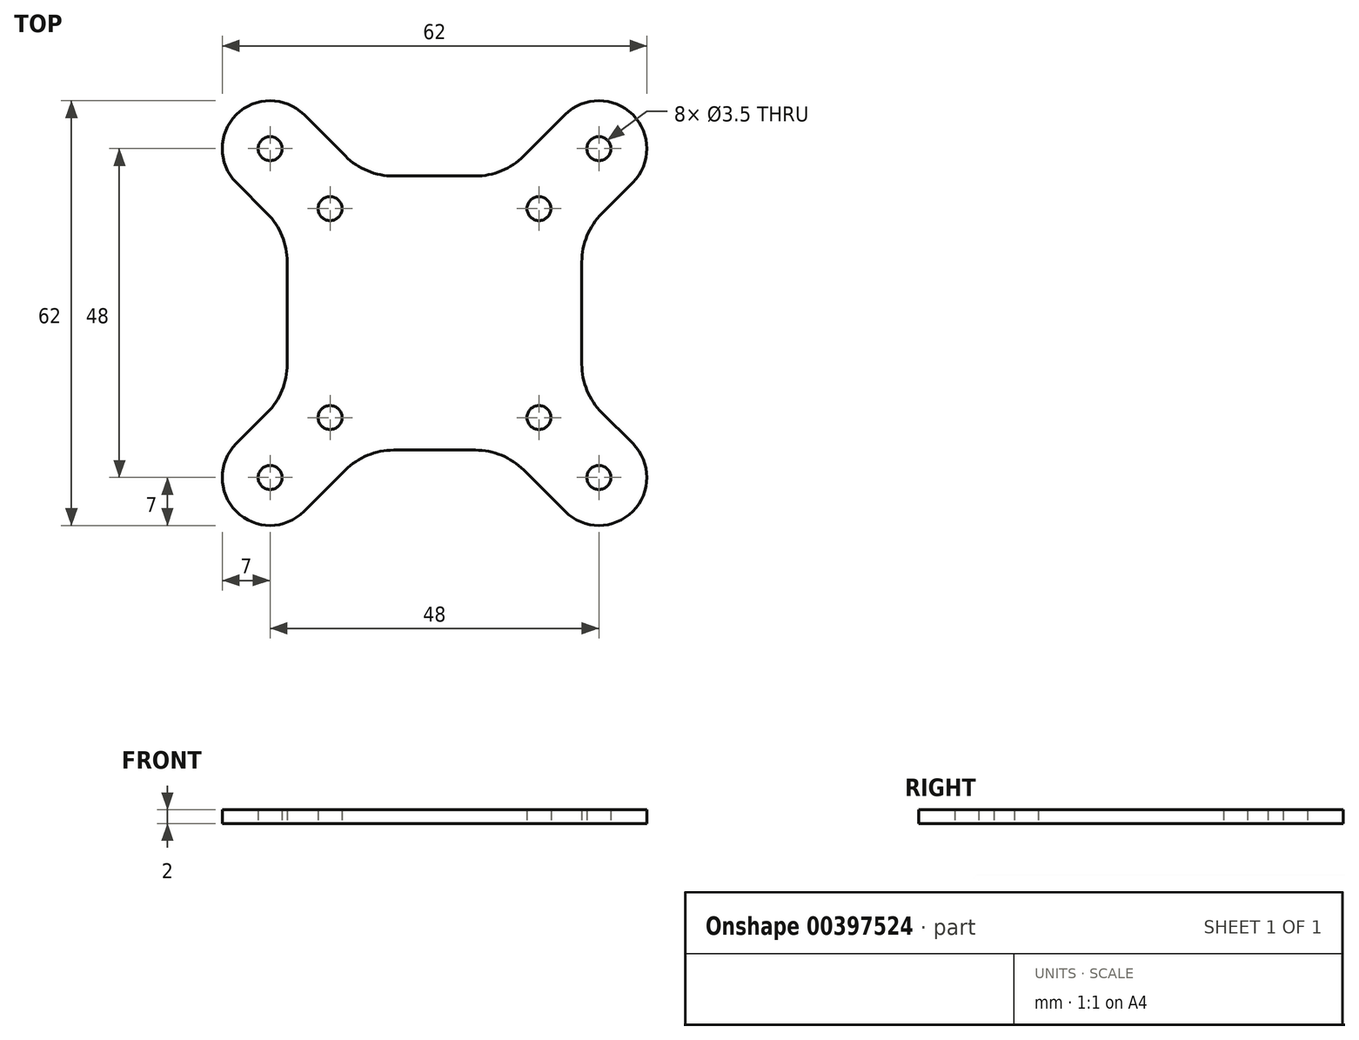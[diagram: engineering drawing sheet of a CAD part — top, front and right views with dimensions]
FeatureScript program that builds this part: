
annotation { "Feature Type Name" : "Feature", "Feature Type Description" : "" }
export const myFeature = defineFeature(function(context is Context, id is Id, definition is map)
    precondition{}
    {
        {
            var Q0;
            Q0=qCreatedBy(makeId("Top.planeOp"),FACE);
            var sketch = newSketch(context, id + "F0", { "sketchPlane" : qUnion([Q0])});
            skCircle(sketch, "E0", {"center": v(-15.25, 15.25) * mm, "radius": 1.75 * mm});
            skCircle(sketch, "E1", {"center": v(-24, 24) * mm, "radius": 1.75 * mm});
            skLineSegment(sketch, "E2", {"start": v(0, 0) * mm, "end": v(-24, 24) * mm, "construction": true});
            skLineSegment(sketch, "E3", {"start": v(-28.95, 19.05) * mm, "end": v(-24.43, 14.53) * mm});
            skLineSegment(sketch, "E4", {"start": v(-19.05, 28.95) * mm, "end": v(-13.03, 22.93) * mm});
            skLineSegment(sketch, "E5", {"start": v(-28.95, 28.95) * mm, "end": v(-28.95, 28.95) * mm});
            skPoint(sketch, "E6.visualSharp", {"position": v(-24, 33.9) * mm});
            skArc(sketch, "E6.filletArc", {"start": v(-19.05, 28.95) * mm, "mid": v(-24, 31) * mm, "end": v(-28.95, 28.95) * mm});
            skPoint(sketch, "E7.visualSharp", {"position": v(-33.9, 24) * mm});
            skArc(sketch, "E7.filletArc", {"start": v(-28.95, 28.95) * mm, "mid": v(-31, 24) * mm, "end": v(-28.95, 19.05) * mm});
            skLineSegment(sketch, "E8", {"start": v(-21.5, 7.46) * mm, "end": v(-21.5, 0) * mm});
            skLineSegment(sketch, "E9", {"start": v(-5.96, 20) * mm, "end": v(0, 20) * mm});
            skPoint(sketch, "E10.visualSharp", {"position": v(-10.1, 20) * mm});
            skArc(sketch, "E10.filletArc", {"start": v(-13.03, 22.93) * mm, "mid": v(-9.79, 20.76) * mm, "end": v(-5.96, 20) * mm});
            skPoint(sketch, "E11.visualSharp", {"position": v(-21.5, 11.6) * mm});
            skArc(sketch, "E11.filletArc", {"start": v(-21.5, 7.46) * mm, "mid": v(-22.26, 11.29) * mm, "end": v(-24.43, 14.53) * mm});
            skPoint(sketch, "E12.MirrorP", {"position": v(33.9, 24) * mm});
            skCircle(sketch, "E13.MirrorC", {"center": v(15.25, 15.25) * mm, "radius": 1.75 * mm});
            skCircle(sketch, "E14.MirrorC", {"center": v(24, 24) * mm, "radius": 1.75 * mm});
            skPoint(sketch, "E15.MirrorP", {"position": v(24, 33.9) * mm});
            skLineSegment(sketch, "E16.MirrorCS", {"start": v(0, 0) * mm, "end": v(24, 24) * mm, "construction": true});
            skPoint(sketch, "E17.MirrorP", {"position": v(10.1, 20) * mm});
            skLineSegment(sketch, "E18.MirrorCS", {"start": v(28.95, 19.05) * mm, "end": v(24.43, 14.53) * mm});
            skLineSegment(sketch, "E19.MirrorCS", {"start": v(19.05, 28.95) * mm, "end": v(13.03, 22.93) * mm});
            skArc(sketch, "E20.MirrorCS", {"start": v(19.05, 28.95) * mm, "mid": v(24, 31) * mm, "end": v(28.95, 28.95) * mm});
            skLineSegment(sketch, "E21.MirrorCS", {"start": v(21.5, 7.46) * mm, "end": v(21.5, 0) * mm});
            skArc(sketch, "E22.MirrorCS", {"start": v(28.95, 28.95) * mm, "mid": v(31, 24) * mm, "end": v(28.95, 19.05) * mm});
            skLineSegment(sketch, "E23.MirrorCS", {"start": v(28.95, 28.95) * mm, "end": v(28.95, 28.95) * mm});
            skArc(sketch, "E24.MirrorCS", {"start": v(21.5, 7.46) * mm, "mid": v(22.26, 11.29) * mm, "end": v(24.43, 14.53) * mm});
            skLineSegment(sketch, "E25.MirrorCS", {"start": v(5.96, 20) * mm, "end": v(0, 20) * mm});
            skPoint(sketch, "E26.MirrorP", {"position": v(21.5, 11.6) * mm});
            skArc(sketch, "E27.MirrorCS", {"start": v(13.03, 22.93) * mm, "mid": v(9.79, 20.76) * mm, "end": v(5.96, 20) * mm});
            skArc(sketch, "E28.MirrorCS", {"start": v(19.05, -28.95) * mm, "mid": v(24, -31) * mm, "end": v(28.95, -28.95) * mm});
            skLineSegment(sketch, "E29.MirrorCS", {"start": v(28.95, -28.95) * mm, "end": v(28.95, -28.95) * mm});
            skArc(sketch, "E30.MirrorCS", {"start": v(28.95, -28.95) * mm, "mid": v(31, -24) * mm, "end": v(28.95, -19.05) * mm});
            skLineSegment(sketch, "E31.MirrorCS", {"start": v(5.96, -20) * mm, "end": v(0, -20) * mm});
            skCircle(sketch, "E32.MirrorC", {"center": v(24, -24) * mm, "radius": 1.75 * mm});
            skCircle(sketch, "E33.MirrorC", {"center": v(15.25, -15.25) * mm, "radius": 1.75 * mm});
            skArc(sketch, "E34.MirrorCS", {"start": v(-21.5, -7.46) * mm, "mid": v(-22.26, -11.29) * mm, "end": v(-24.43, -14.53) * mm});
            skArc(sketch, "E35.MirrorCS", {"start": v(-13.03, -22.93) * mm, "mid": v(-9.79, -20.76) * mm, "end": v(-5.96, -20) * mm});
            skLineSegment(sketch, "E36.MirrorCS", {"start": v(-5.96, -20) * mm, "end": v(0, -20) * mm});
            skLineSegment(sketch, "E37.MirrorCS", {"start": v(-21.5, -7.46) * mm, "end": v(-21.5, 0) * mm});
            skArc(sketch, "E38.MirrorCS", {"start": v(-28.95, -28.95) * mm, "mid": v(-31, -24) * mm, "end": v(-28.95, -19.05) * mm});
            skArc(sketch, "E39.MirrorCS", {"start": v(-19.05, -28.95) * mm, "mid": v(-24, -31) * mm, "end": v(-28.95, -28.95) * mm});
            skLineSegment(sketch, "E40.MirrorCS", {"start": v(-19.05, -28.95) * mm, "end": v(-13.03, -22.93) * mm});
            skPoint(sketch, "E41.MirrorP", {"position": v(10.1, -20) * mm});
            skLineSegment(sketch, "E42.MirrorCS", {"start": v(-28.95, -19.05) * mm, "end": v(-24.43, -14.53) * mm});
            skLineSegment(sketch, "E43.MirrorCS", {"start": v(0, 0) * mm, "end": v(-24, -24) * mm, "construction": true});
            skPoint(sketch, "E44.MirrorP", {"position": v(-24, -33.9) * mm});
            skPoint(sketch, "E45.MirrorP", {"position": v(21.5, -11.6) * mm});
            skLineSegment(sketch, "E46.MirrorCS", {"start": v(19.05, -28.95) * mm, "end": v(13.03, -22.93) * mm});
            skLineSegment(sketch, "E47.MirrorCS", {"start": v(-28.95, -28.95) * mm, "end": v(-28.95, -28.95) * mm});
            skCircle(sketch, "E48.MirrorC", {"center": v(-15.25, -15.25) * mm, "radius": 1.75 * mm});
            skCircle(sketch, "E49.MirrorC", {"center": v(-24, -24) * mm, "radius": 1.75 * mm});
            skPoint(sketch, "E50.MirrorP", {"position": v(33.9, -24) * mm});
            skLineSegment(sketch, "E51.MirrorCS", {"start": v(28.95, -19.05) * mm, "end": v(24.43, -14.53) * mm});
            skLineSegment(sketch, "E52.MirrorCS", {"start": v(0, 0) * mm, "end": v(24, -24) * mm, "construction": true});
            skLineSegment(sketch, "E53.MirrorCS", {"start": v(21.5, -7.46) * mm, "end": v(21.5, 0) * mm});
            skPoint(sketch, "E54.MirrorP", {"position": v(-33.9, -24) * mm});
            skPoint(sketch, "E55.MirrorP", {"position": v(-10.1, -20) * mm});
            skPoint(sketch, "E56.MirrorP", {"position": v(-21.5, -11.6) * mm});
            skArc(sketch, "E57.MirrorCS", {"start": v(21.5, -7.46) * mm, "mid": v(22.26, -11.29) * mm, "end": v(24.43, -14.53) * mm});
            skArc(sketch, "E58.MirrorCS", {"start": v(13.03, -22.93) * mm, "mid": v(9.79, -20.76) * mm, "end": v(5.96, -20) * mm});
            skPoint(sketch, "E59.MirrorP", {"position": v(24, -33.9) * mm});
            skSolve(sketch);
        }
        {
            var Q0;
            Q0=makeQuery(id+"F0.imprint","IMPRINT",FACE,{"disambiguationData":[TD([[makeQuery(id+"F0.imprint","IMPRINT",EDGE,{"derivedFrom":sQuery(id+"F0.wireOp",EDGE,"E0")}),-1.0]])]});
            extrude(context, id + "F1", {"entities" : qUnion([Q0]), "depth" : 2 * mm});
        }
    });
